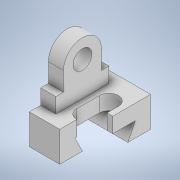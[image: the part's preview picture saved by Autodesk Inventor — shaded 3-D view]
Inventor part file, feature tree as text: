
AUTODESK INVENTOR PART (.ipt)
format: ipt  version: 2022 (Build 260153000, 153)  size: 163,840 bytes
history: native  units: mm
features: extrude x5, sketch x5, other x2
ambient origin geometry x8: Origin, YZ Plane, XZ Plane, XY Plane, X Axis, Y Axis, Z Axis, Center Point
bodies: Body1 (feature_tree)
feature tree (12):
  other  "Твердое тело1"
  extrude  "Выдавливание1"  Depth=100.0mm
  extrude  "Выдавливание2"  Depth=60.0mm
  extrude  "Выдавливание5"  Depth=100.0mm
  extrude  "Выдавливание6"  Depth=40.0mm TaperAngle=0.0deg
  other  "РабПлоскость1"
  extrude  "Выдавливание7"  Depth=40.0mm
  sketch  "Эскиз1"
  sketch  "Эскиз2"
  sketch  "Эскиз4"
  sketch  "Эскиз5"
  sketch  "Эскиз6"
